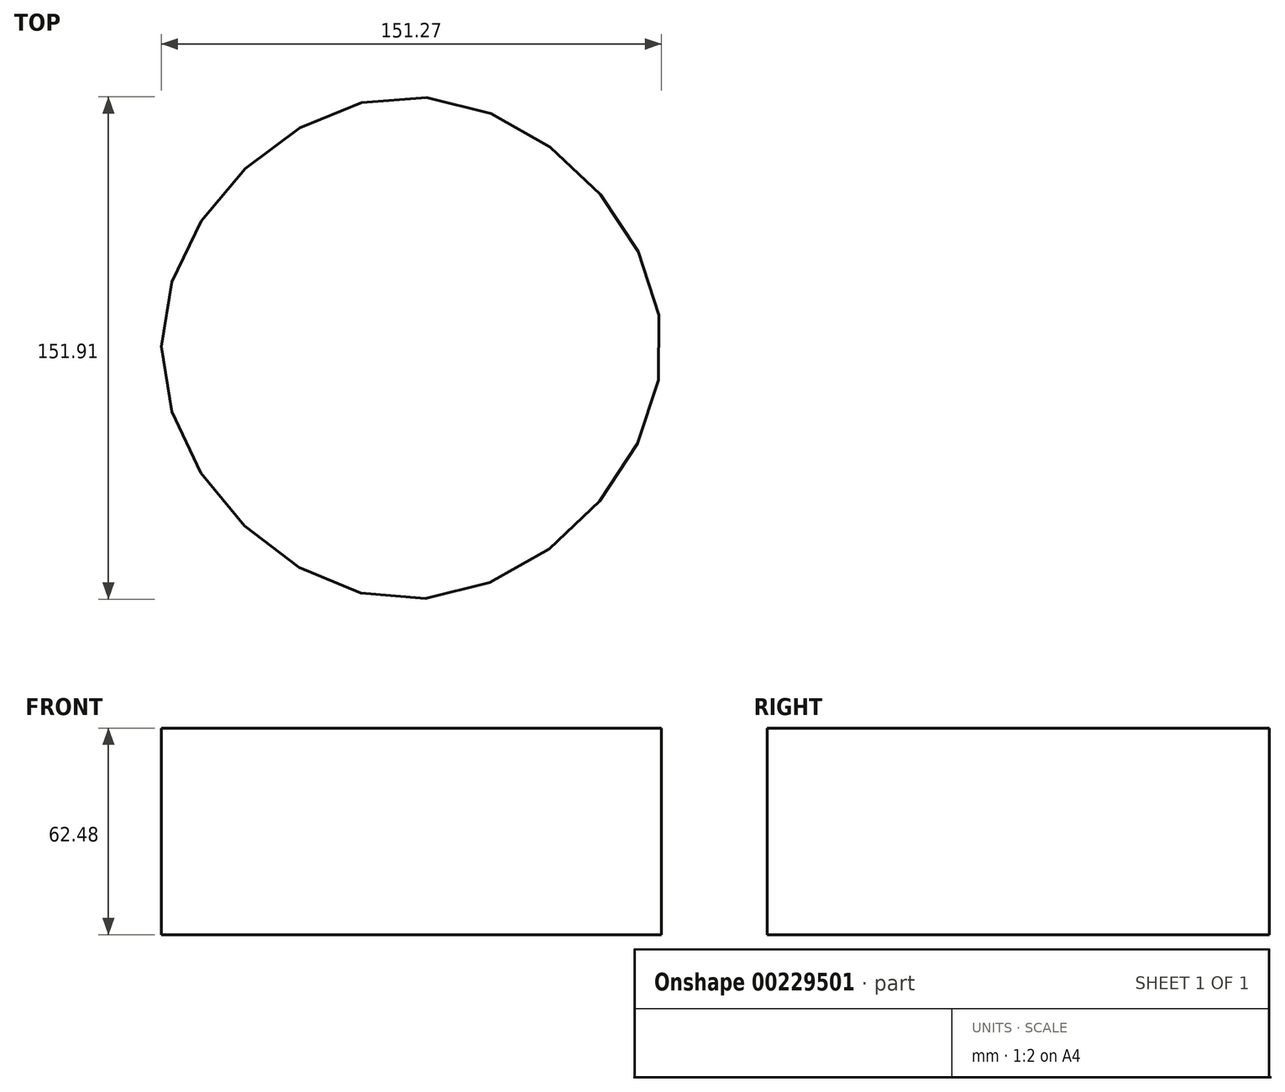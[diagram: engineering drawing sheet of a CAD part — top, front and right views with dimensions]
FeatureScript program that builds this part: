
annotation { "Feature Type Name" : "Feature", "Feature Type Description" : "" }
export const myFeature = defineFeature(function(context is Context, id is Id, definition is map)
    precondition{}
    {
        {
            var Q0;
            Q0=qCreatedBy(makeId("Top.planeOp"),FACE);
            var sketch = newSketch(context, id + "F0", { "sketchPlane" : qUnion([Q0])});
            skFitSpline(sketch, "E0", {"points": [v(-74.89, 0) * mm, v(0, 75.53) * mm, v(76.38, 0) * mm, v(0, -76.38) * mm, v(-74.89, 0) * mm]});
            skSolve(sketch);
        }
        {
            var Q0;
            Q0 = qSketchRegion(id + "F0", true);
            extrude(context, id + "F1", {"entities" : qUnion([Q0]), "depth" : 62.48 * mm});
        }
    });
